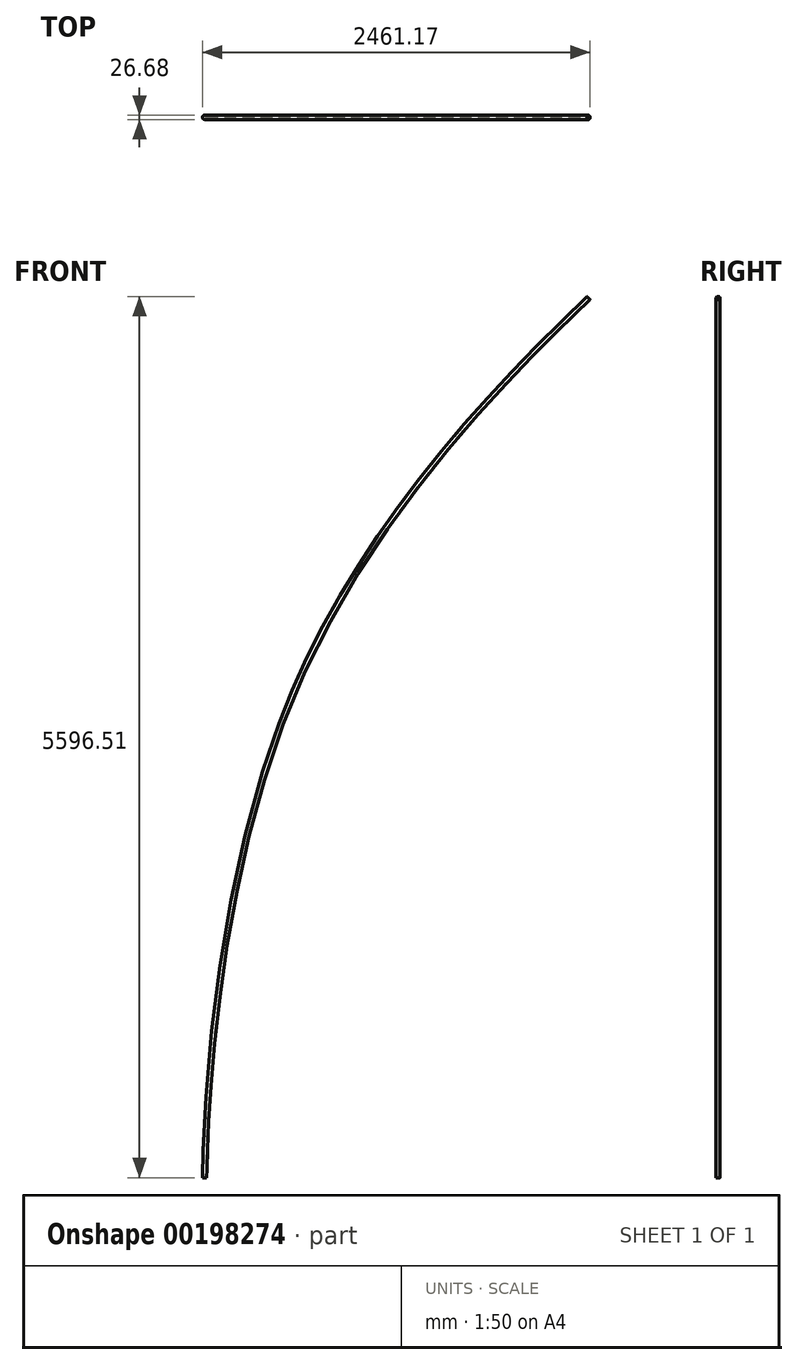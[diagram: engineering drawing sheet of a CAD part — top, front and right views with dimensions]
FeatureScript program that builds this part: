
annotation { "Feature Type Name" : "Feature", "Feature Type Description" : "" }
export const myFeature = defineFeature(function(context is Context, id is Id, definition is map)
    precondition{}
    {
        {
            var Q0;
            Q0=qCreatedBy(makeId("Front.planeOp"),FACE);
            var sketch = newSketch(context, id + "F0", { "sketchPlane" : qUnion([Q0])});
            skFitSpline(sketch, "E0", {"points": [v(0, 0) * mm, v(531.55, 3001.3) * mm, v(2438.4, 5587.08) * mm], "startDerivative": vector(0, 512.83) * mm, "endDerivative": vector(1805.03, 1805.03) * mm});
            skLineSegment(sketch, "E1", {"start": v(2438.4, 5587.08) * mm, "end": v(2133.6, 5587.08) * mm, "construction": true});
            skSolve(sketch);
        }
        {
            var Q0;
            Q0=qCreatedBy(makeId("Top.planeOp"),FACE);
            var sketch = newSketch(context, id + "F1", { "sketchPlane" : qUnion([Q0])});
            skCircle(sketch, "E2", {"center": v(0, 0) * mm, "radius": 13.34 * mm});
            skCircle(sketch, "E3", {"center": v(0, 0) * mm, "radius": 10.71 * mm});
            skSolve(sketch);
        }
        {
            var Q0;
            Q0=makeQuery(id+"F1.imprint","IMPRINT",FACE,{"disambiguationData":[TD([[makeQuery(id+"F1.imprint","IMPRINT",EDGE,{"derivedFrom":sQuery(id+"F1.wireOp",EDGE,"E2")}),1.0]])]});
            var Q1;
            Q1=sQuery(id+"F1.wireOp",EDGE,"E2");
            var Q2;
            Q2=sQuery(id+"F0.wireOp",EDGE,"E0");
            sweep(context, id + "F2", {"profiles" : qUnion([Q0]), "surfaceProfiles" : qUnion([Q1]), "path" : qUnion([Q2])});
        }
    });
